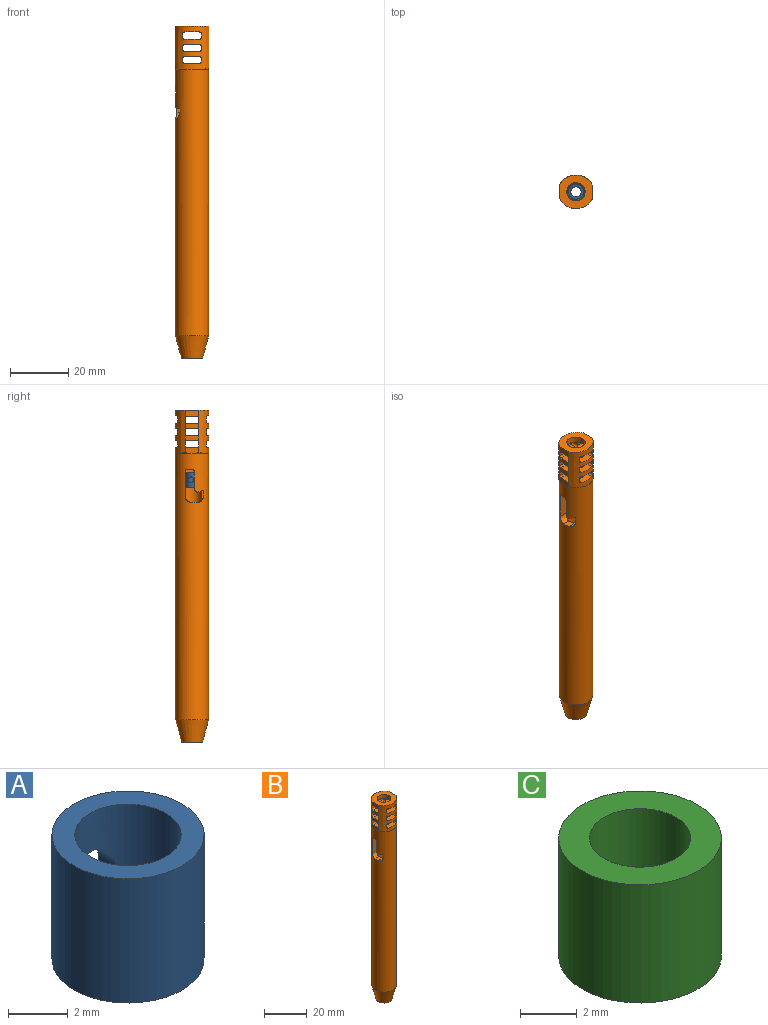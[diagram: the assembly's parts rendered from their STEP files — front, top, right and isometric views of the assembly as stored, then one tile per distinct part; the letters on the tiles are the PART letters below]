
ASSEMBLY  parts=3 mates=1
PART A: 5 faces, bbox 5.1x5.1x5.1 mm
  f0: cylinder r=1.78mm len=5.08mm, axis (0,0,-1), area 53.8mm2, adj f2,f3,f4
  f1: cylinder r=2.54mm len=5.08mm, axis (0,0,-1), area 78.2mm2, adj f2,f3,f4
  f2: plane 5.08x5.08mm, normal (0,0,1), area 10.3mm2, adj f0,f1
  f3: plane 5.08x5.08mm, normal (0,0,-1), area 10.3mm2, adj f0,f1
  f4: cylinder r=0.95mm len=1.91mm, axis (0,-1,0), area 4.8mm2, adj f0,f1
PART B: 130 faces, bbox 12.4x12.4x114.4 mm
  f0: plane 4.53x2.65mm, normal (-1,0,0), area 8.6mm2, adj f33,f34,f73,f74,f96,f97,f98
  f1: plane 4.52x2.86mm, normal (-1,0,0), area 7.5mm2, adj f73,f74,f76,f77,f79,f84,f85,f87
  f2: plane 4.52x2.97mm, normal (-1,0,0), area 8mm2, adj f73,f74,f88,f89,f90,f92,f93,f95
  f3: cylinder r=0.64mm len=3.46mm, axis (0,1,0), area 3mm2, adj f4,f23,f62,f74,f91,f98
  f4: plane 2.65x1.27mm, normal (1,0,0), area 3.4mm2, adj f3,f38,f74,f91,f92
  f5: plane 2.65x1.27mm, normal (1,0,0), area 3.4mm2, adj f39,f43,f74,f83,f90
  f6: cylinder r=0.64mm len=3.25mm, axis (0,1,0), area 2.9mm2, adj f7,f30,f74,f78,f79
  f7: plane 2.66x1.27mm, normal (1,0,0), area 3.4mm2, adj f6,f8,f74,f78,f81
  f8: cylinder r=0.64mm len=3.89mm, axis (0,1,0), area 3.2mm2, adj f7,f18,f31,f74,f80,f81
  f9: plane 4.53x2.65mm, normal (1,0,0), area 8.6mm2, adj f48,f49,f73,f74,f115,f117,f121
  f10: plane 4.52x2.86mm, normal (1,0,0), area 7.5mm2, adj f73,f74,f100,f101,f105,f108,f110,f112
  f11: plane 4.52x2.97mm, normal (1,0,0), area 8mm2, adj f73,f74,f107,f111,f114,f116,f119,f122
  f12: plane 2.65x1.27mm, normal (-1,0,0), area 3.4mm2, adj f13,f50,f74,f120,f122
  f13: cylinder r=0.64mm len=3.46mm, axis (0,1,0), area 3mm2, adj f12,f23,f62,f74,f120,f121
  f14: plane 2.65x1.27mm, normal (-1,0,0), area 3.4mm2, adj f54,f58,f74,f113,f114
  f15: cylinder r=0.64mm len=3.89mm, axis (0,1,0), area 3.2mm2, adj f16,f18,f31,f74,f99,f106
  f16: plane 2.66x1.27mm, normal (-1,0,0), area 3.4mm2, adj f15,f17,f74,f104,f106
  f17: cylinder r=0.64mm len=3.25mm, axis (0,1,0), area 2.9mm2, adj f16,f30,f74,f104,f105
  f18: cylinder r=3.17mm len=6.35mm, axis (0,0,-1), area 41.2mm2, adj f8,f15,f19,f29,f31,f45,f61,f80
  f19: plane 11.43x11.43mm, normal (0,0,1), area 77mm2, adj f18,f32,f47,f73,f74
  f20: plane 5.08x3.81mm, normal (0,0,-1), area 14mm2, adj f36,f53,f71,f73
  f21: plane 5.08x3.81mm, normal (0,0,1), area 14mm2, adj f37,f52,f62,f73
  f22: plane 5.08x3.81mm, normal (0,0,-1), area 14mm2, adj f38,f50,f71,f74
  f23: plane 5.08x3.81mm, normal (0,0,1), area 14mm2, adj f3,f13,f62,f74
  f24: plane 5.08x3.81mm, normal (0,0,1), area 14mm2, adj f42,f56,f71,f73
  f25: plane 5.08x3.81mm, normal (0,0,-1), area 14mm2, adj f41,f57,f72,f73
  f26: plane 5.08x3.81mm, normal (0,0,1), area 14mm2, adj f39,f58,f71,f74
  f27: plane 5.08x3.81mm, normal (0,0,-1), area 14mm2, adj f43,f54,f72,f74
  f28: plane 5.08x3.74mm, normal (0,0,1), area 14mm2, adj f46,f59,f72,f73,f76,f101
  f29: plane 5.08x3.81mm, normal (0,0,-1), area 14mm2, adj f18,f45,f61,f73
  f30: plane 5.08x3.74mm, normal (0,0,1), area 14mm2, adj f6,f17,f72,f74,f79,f105
  f31: plane 5.08x3.81mm, normal (0,0,-1), area 14mm2, adj f8,f15,f18,f74
  f32: plane 4.52x2.77mm, normal (-1,0,0), area 9.8mm2, adj f19,f73,f74,f80,f81,f82
  f33: cone r=8.08mm half-angle=45deg, axis (0,0,1), area 2.1mm2, adj f0,f63,f73
  f34: cone r=8.08mm half-angle=45deg, axis (0,0,1), area 2.1mm2, adj f0,f63,f74
  f35: plane 2.65x1.27mm, normal (1,0,0), area 3.4mm2, adj f36,f37,f73,f94,f95
  f36: cylinder r=0.64mm len=3.49mm, axis (0,1,0), area 3mm2, adj f20,f35,f71,f73,f95
  f37: cylinder r=0.64mm len=3.46mm, axis (0,1,0), area 3mm2, adj f21,f35,f62,f73,f94,f96
  f38: cylinder r=0.64mm len=3.49mm, axis (0,1,0), area 3mm2, adj f4,f22,f71,f74,f92
  f39: cylinder r=0.64mm len=3.49mm, axis (0,1,0), area 3mm2, adj f5,f26,f71,f74,f90
  f40: plane 2.65x1.27mm, normal (1,0,0), area 3.4mm2, adj f41,f42,f73,f86,f88
  f41: cylinder r=0.64mm len=3.46mm, axis (0,1,0), area 3mm2, adj f25,f40,f72,f73,f86,f87
  f42: cylinder r=0.64mm len=3.49mm, axis (0,1,0), area 3mm2, adj f24,f40,f71,f73,f88
  f43: cylinder r=0.64mm len=3.46mm, axis (0,1,0), area 3mm2, adj f5,f27,f72,f74,f83,f84
  f44: plane 2.66x1.27mm, normal (1,0,0), area 3.4mm2, adj f45,f46,f73,f75,f82
  f45: cylinder r=0.64mm len=3.89mm, axis (0,1,0), area 3.2mm2, adj f18,f29,f44,f73,f80,f82
  f46: cylinder r=0.64mm len=3.25mm, axis (0,1,0), area 2.9mm2, adj f28,f44,f73,f75,f76
  f47: plane 4.52x2.77mm, normal (1,0,0), area 9.8mm2, adj f19,f73,f74,f99,f103,f106
  f48: cone r=8.08mm half-angle=45deg, axis (0,0,1), area 2.1mm2, adj f9,f63,f73
  f49: cone r=8.08mm half-angle=45deg, axis (0,0,1), area 2.1mm2, adj f9,f63,f74
  f50: cylinder r=0.64mm len=3.49mm, axis (0,1,0), area 3mm2, adj f12,f22,f71,f74,f122
  f51: plane 2.65x1.27mm, normal (-1,0,0), area 3.4mm2, adj f52,f53,f73,f118,f119
  f52: cylinder r=0.64mm len=3.46mm, axis (0,1,0), area 3mm2, adj f21,f51,f62,f73,f117,f118
  f53: cylinder r=0.64mm len=3.49mm, axis (0,1,0), area 3mm2, adj f20,f51,f71,f73,f119
  f54: cylinder r=0.64mm len=3.46mm, axis (0,1,0), area 3mm2, adj f14,f27,f72,f74,f112,f113
  f55: plane 2.65x1.27mm, normal (-1,0,0), area 3.4mm2, adj f56,f57,f73,f109,f111
  f56: cylinder r=0.64mm len=3.49mm, axis (0,1,0), area 3mm2, adj f24,f55,f71,f73,f111
  f57: cylinder r=0.64mm len=3.46mm, axis (0,1,0), area 3mm2, adj f25,f55,f72,f73,f109,f110
  f58: cylinder r=0.64mm len=3.49mm, axis (0,1,0), area 3mm2, adj f14,f26,f71,f74,f114
  f59: cylinder r=0.64mm len=3.25mm, axis (0,1,0), area 2.9mm2, adj f28,f60,f73,f101,f102
  f60: plane 2.66x1.27mm, normal (-1,0,0), area 3.4mm2, adj f59,f61,f73,f102,f103
  f61: cylinder r=0.64mm len=3.89mm, axis (0,1,0), area 3.2mm2, adj f18,f29,f60,f73,f99,f103
  f62: cylinder r=3.17mm len=101.27mm, axis (0,0,-1), area 1967mm2, adj f3,f13,f21,f23,f37,f52,f64,f65
  f63: cylinder r=5.71mm len=91.62mm, axis (0,0,-1), area 3241.7mm2, adj f33,f34,f48,f49,f64,f65,f66,f67
  f64: plane 8.38x3.09mm, normal (0,-1,0), area 25.9mm2, adj f62,f63,f126,f127
  f65: plane 2.84x1.14mm, normal (0,0,-1), area 3mm2, adj f62,f63,f127,f128
  f66: plane 5.89x2.59mm, normal (0,1,0), area 15.2mm2, adj f62,f63,f128,f129
  f67: plane 5.46x2.03mm, normal (0,-0.28,-0.96), area 7.5mm2, adj f62,f63,f68,f70,f129
  f68: plane 4.1x2.06mm, normal (0,1,0), area 8.4mm2, adj f63,f67,f70,f125
  f69: plane 3.21x2.29mm, normal (0,0,1), area 6mm2, adj f62,f63,f125,f126
  f70: plane 3.68x0.81mm, normal (-1,0,0), area 2.5mm2, adj f62,f67,f68,f125
  f71: cylinder r=3.17mm len=6.35mm, axis (0,0,-1), area 33.9mm2, adj f20,f22,f24,f26,f36,f38,f39,f42
  f72: cylinder r=3.17mm len=6.35mm, axis (0,0,-1), area 33mm2, adj f25,f27,f28,f30,f41,f43,f54,f57
  f73: extruded ~15.06x11.43mm, area 160.5mm2, adj f0,f1,f2,f9,f10,f11,f19,f20
  f74: extruded ~15.06x11.43mm, area 160.5mm2, adj f0,f1,f2,f3,f4,f5,f6,f7
  f75: plane 2.55x1.27mm, normal (0,-1,0), area 3.2mm2, adj f44,f46,f73,f76,f82
  f76: cylinder r=0.64mm len=3.23mm, axis (1,0,0), area 2.9mm2, adj f1,f28,f46,f72,f75,f77
  f77: plane 3.25x2.99mm, normal (0,0,1), area 8.7mm2, adj f1,f72,f76,f79
  f78: plane 2.55x1.27mm, normal (0,1,0), area 3.2mm2, adj f6,f7,f74,f79,f81
  f79: cylinder r=0.64mm len=3.23mm, axis (1,0,0), area 2.9mm2, adj f1,f6,f30,f72,f77,f78
  f80: plane 3.25x2.83mm, normal (0,0,-1), area 8.7mm2, adj f8,f18,f32,f45,f81,f82
  f81: cylinder r=0.64mm len=2.83mm, axis (1,0,0), area 2.7mm2, adj f7,f8,f32,f78,f80
  f82: cylinder r=0.64mm len=2.83mm, axis (1,0,0), area 2.7mm2, adj f32,f44,f45,f75,f80
  f83: plane 2.54x1.27mm, normal (0,1,0), area 3.2mm2, adj f5,f43,f74,f84,f90
  f84: cylinder r=0.64mm len=3.07mm, axis (1,0,0), area 2.8mm2, adj f1,f43,f72,f83,f85
  f85: plane 3.25x2.99mm, normal (0,0,-1), area 8.7mm2, adj f1,f72,f84,f87
  f86: plane 2.54x1.27mm, normal (0,-1,0), area 3.2mm2, adj f40,f41,f73,f87,f88
  f87: cylinder r=0.64mm len=3.07mm, axis (1,0,0), area 2.8mm2, adj f1,f41,f72,f85,f86
  f88: cylinder r=0.64mm len=3.05mm, axis (1,0,0), area 2.7mm2, adj f2,f40,f42,f71,f86,f89
  f89: plane 3.25x2.99mm, normal (0,0,1), area 8.7mm2, adj f2,f71,f88,f90
  f90: cylinder r=0.64mm len=3.05mm, axis (1,0,0), area 2.7mm2, adj f2,f5,f39,f71,f83,f89
  f91: plane 2.54x1.27mm, normal (0,1,0), area 3.2mm2, adj f3,f4,f74,f92,f98
  f92: cylinder r=0.64mm len=3.05mm, axis (1,0,0), area 2.7mm2, adj f2,f4,f38,f71,f91,f93
  f93: plane 3.25x2.99mm, normal (0,0,-1), area 8.7mm2, adj f2,f71,f92,f95
  f94: plane 2.54x1.27mm, normal (0,-1,0), area 3.2mm2, adj f35,f37,f73,f95,f96
  f95: cylinder r=0.64mm len=3.05mm, axis (1,0,0), area 2.7mm2, adj f2,f35,f36,f71,f93,f94
  f96: cylinder r=0.64mm len=3.07mm, axis (1,0,0), area 2.8mm2, adj f0,f37,f62,f94,f97
  f97: plane 3.25x2.99mm, normal (0,0,1), area 8.7mm2, adj f0,f62,f96,f98
  f98: cylinder r=0.64mm len=3.07mm, axis (1,0,0), area 2.8mm2, adj f0,f3,f62,f91,f97
  f99: plane 3.25x2.83mm, normal (0,0,-1), area 8.7mm2, adj f15,f18,f47,f61,f103,f106
  f100: plane 3.25x2.99mm, normal (0,0,1), area 8.7mm2, adj f10,f72,f101,f105
  f101: cylinder r=0.64mm len=3.23mm, axis (1,0,0), area 2.9mm2, adj f10,f28,f59,f72,f100,f102
  f102: plane 2.55x1.27mm, normal (0,-1,0), area 3.2mm2, adj f59,f60,f73,f101,f103
  f103: cylinder r=0.64mm len=2.83mm, axis (1,0,0), area 2.7mm2, adj f47,f60,f61,f99,f102
  f104: plane 2.55x1.27mm, normal (0,1,0), area 3.2mm2, adj f16,f17,f74,f105,f106
  f105: cylinder r=0.64mm len=3.23mm, axis (1,0,0), area 2.9mm2, adj f10,f17,f30,f72,f100,f104
  f106: cylinder r=0.64mm len=2.83mm, axis (1,0,0), area 2.7mm2, adj f15,f16,f47,f99,f104
  f107: plane 3.25x2.99mm, normal (0,0,1), area 8.7mm2, adj f11,f71,f111,f114
  f108: plane 3.25x2.99mm, normal (0,0,-1), area 8.7mm2, adj f10,f72,f110,f112
  f109: plane 2.54x1.27mm, normal (0,-1,0), area 3.2mm2, adj f55,f57,f73,f110,f111
  f110: cylinder r=0.64mm len=3.07mm, axis (1,0,0), area 2.8mm2, adj f10,f57,f72,f108,f109
  f111: cylinder r=0.64mm len=3.05mm, axis (1,0,0), area 2.7mm2, adj f11,f55,f56,f71,f107,f109
  f112: cylinder r=0.64mm len=3.07mm, axis (1,0,0), area 2.8mm2, adj f10,f54,f72,f108,f113
  f113: plane 2.54x1.27mm, normal (0,1,0), area 3.2mm2, adj f14,f54,f74,f112,f114
  f114: cylinder r=0.64mm len=3.05mm, axis (1,0,0), area 2.7mm2, adj f11,f14,f58,f71,f107,f113
  f115: plane 3.25x2.99mm, normal (0,0,1), area 8.7mm2, adj f9,f62,f117,f121
  f116: plane 3.25x2.99mm, normal (0,0,-1), area 8.7mm2, adj f11,f71,f119,f122
  f117: cylinder r=0.64mm len=3.07mm, axis (1,0,0), area 2.8mm2, adj f9,f52,f62,f115,f118
  f118: plane 2.54x1.27mm, normal (0,-1,0), area 3.2mm2, adj f51,f52,f73,f117,f119
  f119: cylinder r=0.64mm len=3.05mm, axis (1,0,0), area 2.7mm2, adj f11,f51,f53,f71,f116,f118
  f120: plane 2.54x1.27mm, normal (0,1,0), area 3.2mm2, adj f12,f13,f74,f121,f122
  f121: cylinder r=0.64mm len=3.07mm, axis (1,0,0), area 2.8mm2, adj f9,f13,f62,f115,f120
  f122: cylinder r=0.64mm len=3.05mm, axis (1,0,0), area 2.7mm2, adj f11,f12,f50,f71,f116,f120
  f123: plane 7.37x7.37mm, normal (0,0,-1), area 10.9mm2, adj f62,f124
  f124: cone r=5.71mm half-angle=14.9deg, axis (0,0,1), area 232.8mm2, adj f63,f123
  f125: cylinder r=2.03mm len=5.37mm, axis (1,0,0), area 12.6mm2, adj f62,f63,f68,f69,f70
  f126: cylinder r=2.03mm len=3.59mm, axis (-1,0,0), area 9.1mm2, adj f62,f63,f64,f69
  f127: cylinder r=1.02mm len=3.44mm, axis (-1,0,0), area 4.7mm2, adj f62,f63,f64,f65
  f128: cylinder r=1.02mm len=2.64mm, axis (-1,0,0), area 4.1mm2, adj f62,f63,f65,f66
  f129: cylinder r=1.02mm len=3.28mm, axis (-1,0,0), area 5.1mm2, adj f62,f63,f66,f67
PART C: 4 faces, bbox 5.7x5.7x5.1 mm
  f0: cylinder r=1.78mm len=5.08mm, axis (0,0,-1), area 56.8mm2, adj f2,f3
  f1: cylinder r=2.86mm len=5.72mm, axis (0,0,-1), area 91.2mm2, adj f2,f3
  f2: plane 5.72x5.72mm, normal (0,0,1), area 15.7mm2, adj f0,f1
  f3: plane 5.72x5.72mm, normal (0,0,-1), area 15.7mm2, adj f0,f1
PLACE A rot(axis=(0,0,1),80.8deg) t=(14.19,1.66,86.09)mm
PLACE B t=(14.19,1.66,49.13)mm
PLACE C rot(axis=(0,1,0),180deg) t=(14.19,1.66,52.85)mm
MATE cylindrical A.f1 <-> B.f33  axis (0,0,1) through (14.19,1.66,91.17)mm
